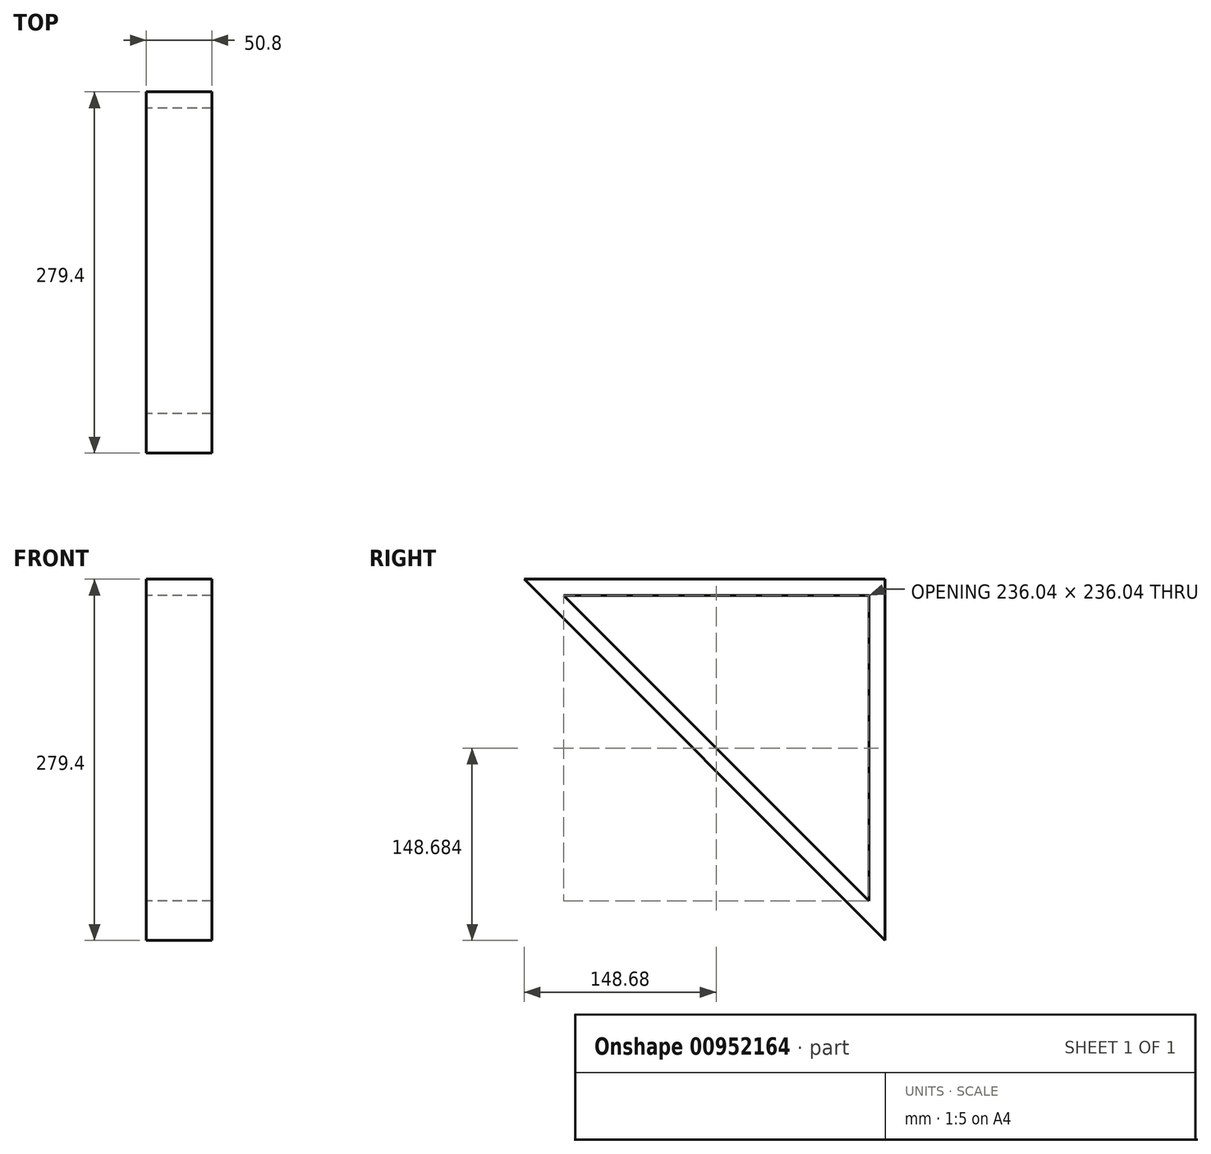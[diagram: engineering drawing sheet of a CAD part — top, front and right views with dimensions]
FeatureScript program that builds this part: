
annotation { "Feature Type Name" : "Feature", "Feature Type Description" : "" }
export const myFeature = defineFeature(function(context is Context, id is Id, definition is map)
    precondition{}
    {
        {
            var Q0;
            Q0=qCreatedBy(makeId("Right.planeOp"),FACE);
            var sketch = newSketch(context, id + "F0", { "sketchPlane" : qUnion([Q0])});
            skLineSegment(sketch, "E0.bottom", {"start": v(0, 6.04) * mm, "end": v(12.7, 6.04) * mm});
            skLineSegment(sketch, "E0.top", {"start": v(0, -260.66) * mm, "end": v(12.7, -260.66) * mm});
            skLineSegment(sketch, "E0.left", {"start": v(0, 6.04) * mm, "end": v(0, -260.66) * mm});
            skLineSegment(sketch, "E0.right", {"start": v(12.7, 6.04) * mm, "end": v(12.7, -260.66) * mm});
            skLineSegment(sketch, "E1.bottom", {"start": v(12.7, 6.04) * mm, "end": v(-254, 6.04) * mm});
            skLineSegment(sketch, "E1.top", {"start": v(12.7, -6.66) * mm, "end": v(-254, -6.66) * mm});
            skLineSegment(sketch, "E1.left", {"start": v(12.7, 6.04) * mm, "end": v(12.7, -6.66) * mm});
            skLineSegment(sketch, "E1.right", {"start": v(-254, 6.04) * mm, "end": v(-254, -6.66) * mm});
            skLineSegment(sketch, "E2", {"start": v(-254, -6.66) * mm, "end": v(0, -260.66) * mm});
            skLineSegment(sketch, "E3", {"start": v(-236.04, -6.66) * mm, "end": v(0, -242.7) * mm});
            skLineSegment(sketch, "E4.bottom", {"start": v(12.7, -260.66) * mm, "end": v(-12.7, -259.73) * mm});
            skLineSegment(sketch, "E5.left", {"start": v(-254, 6.04) * mm, "end": v(-254, -18.43) * mm});
            skLineSegment(sketch, "E6", {"start": v(-254, -6.66) * mm, "end": v(-266.7, 6.04) * mm});
            skLineSegment(sketch, "E7", {"start": v(-266.7, 6.04) * mm, "end": v(-254, 6.04) * mm});
            skLineSegment(sketch, "E8", {"start": v(0, -260.66) * mm, "end": v(15.87, -276.52) * mm});
            skLineSegment(sketch, "E9", {"start": v(12.7, -260.66) * mm, "end": v(12.7, -276.77) * mm});
            skLineSegment(sketch, "E10", {"start": v(12.7, -273.36) * mm, "end": v(15.87, -276.52) * mm});
            skSolve(sketch);
        }
        {
            var Q0;
            Q0 = qSketchRegion(id + "F0", true);
            extrude(context, id + "F1", {"entities" : qUnion([Q0]), "depth" : 25.4 * mm, "offsetDistance" : 25.4 * mm, "hasSecondDirection" : true, "secondDirectionOppositeDirection" : true, "secondDirectionDepth" : 25.4 * mm});
        }
        {
            var Q0;
            Q0 = qSketchRegion(id + "F0", true);
            extrude(context, id + "F2", {"entities" : qUnion([Q0]), "operationType" : NewBodyOperationType.ADD, "depth" : 25.4 * mm, "offsetDistance" : 25.4 * mm});
        }
    });
